# Revit family: Reece_Vanity_Posh_Bristol
name_source: partatom
category: Casework
revit_build: Autodesk Revit 2018 (Build: 20190510_1515(x64)
units: mm (PartAtom-declared; Revit-internal decimal feet)

## family parameters
Always vertical = Yes
Cut with Voids When Loaded = Yes
Room Calculation Point = Yes
Shared = Yes
Work Plane-Based = Yes

## types (1)
- Reece_All_Types
    Default Elevation = 0 mm  [stored 0 ft]
    Description = -
    Disclaimer = THIS FILE IS THE PROPERTY OF THE REECE GROUP. IT MAY NOT BE REPRODUCED, REVERSE-ENGINEERED OR MODIFIED. ANY REPUBLICATION, TRANSMISSION OR DISTRIBUTION FOR THE PURPOSE OF COMMERCIALLY EXPLOITING THE FILES IS PROHIBITED.
    Finish = Please refer to Colour, Finish and Material Variations Document in the Reece_Product_Finishes_Web Page parameter for more information.
    Keynote = Product #, Reece_Vanity_Posh_Bristol - Reece_All_Types
    Manufacturer = Posh
    Model = Bristol MK2
    Reece_Basin_Bowl_430_Visibility = No
    Reece_Basin_Bowl_480_Visibility = Yes
    Reece_Basin_Bowl_510_Visibility = No
    Reece_Basin_Outlet = 40 mm  [stored 0.131234 ft]
    Reece_Basin_Taphole 3 = No
    Reece_Basin_Taphole_3_Visibility = No
    Reece_Benchtop = Yes
    Reece_Benchtop_Depth = 460 mm  [stored 1.50919 ft]
    Reece_Benctop_Width = 750 mm  [stored 2.46063 ft]
    Reece_Cabinet_LH_Drawer = No
    Reece_Cabinet_RH_Drawer = Yes
    Reece_Cabinet_Width = 725 mm  [stored 2.37861 ft]
    Reece_Centre_Bowl = Yes
    Reece_Detail_Disclaimer = THIS FILE IS THE PROPERTY OF THE REECE GROUP. IT MAY NOT BE REPRODUCED, REVERSE-ENGINEERED OR MODIFIED. ANY REPUBLICATION, TRANSMISSION OR DISTRIBUTION FOR THE PURPOSE OF COMMERCIALLY EXPLOITING THE FILES IS PROHIBITED.
    Reece_Floor_Mount = No
    Reece_Material_Cabinet = Reece_Polyurethane_White
    Reece_Material_Handle = Reece_Metal_Bright Chrome
    Reece_Material_Main = Reece_Vitreous China_White
    Reece_Material_Secondary = Reece_Brass_Chrome
    Reece_Material_Shelf = Reece_Polyurethane_White
    Reece_Overall_Capacity = Please Refer to Manufacturer's Specifications
    Reece_Overall_Depth = 460 mm  [stored 1.50919 ft]
    Reece_Overall_Height = 543 mm  [stored 1.7815 ft]
    Reece_Overall_Width = 750 mm  [stored 2.46063 ft]
    Reece_Product_Brand = Posh
    Reece_Product_Sub Brand = Bristol MK2
    Reece_Product_Type = Vanity
    Type Comments = Vanity
    URL = -

note: [stored X ft] marks values corroborated as IEEE doubles in the binary element streams (Revit-internal decimal feet)

## geometry (parser evidence)
native form markers: Sweep x17
no freeform markers — native parametric forms only
